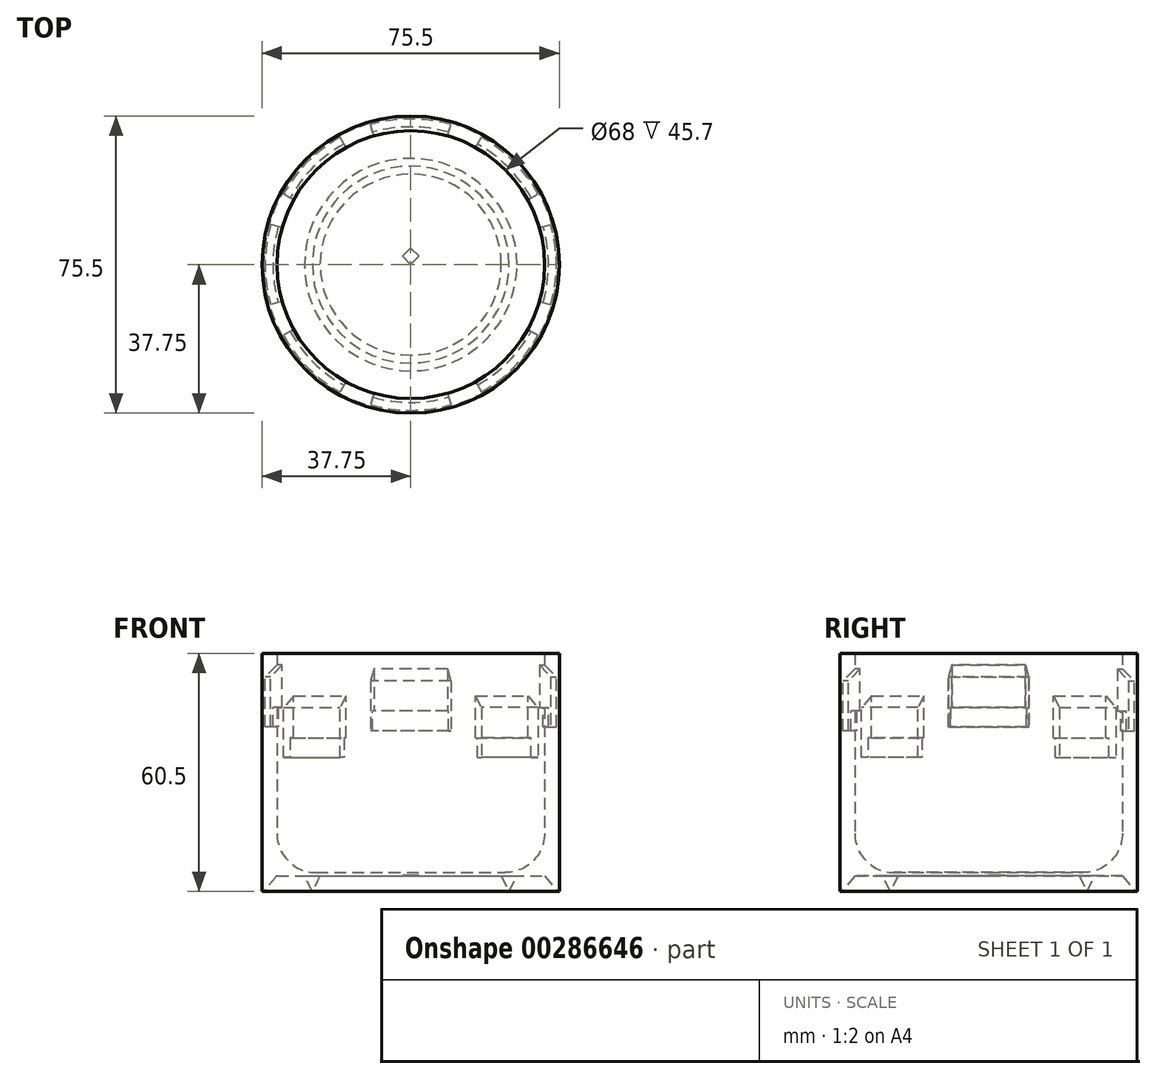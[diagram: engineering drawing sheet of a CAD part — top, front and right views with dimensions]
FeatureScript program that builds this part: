
annotation { "Feature Type Name" : "Feature", "Feature Type Description" : "" }
export const myFeature = defineFeature(function(context is Context, id is Id, definition is map)
    precondition{}
    {
        {
            var Q0;
            Q0=qCreatedBy(makeId("Front.planeOp"),FACE);
            var sketch = newSketch(context, id + "F0", { "sketchPlane" : qUnion([Q0])});
            skLineSegment(sketch, "E0", {"start": v(-34, 0) * mm, "end": v(-34, -4) * mm});
            skLineSegment(sketch, "E1", {"start": v(-34, -4) * mm, "end": v(-40, -4) * mm});
            skLineSegment(sketch, "E2", {"start": v(-40, -4) * mm, "end": v(-40, 21) * mm});
            skLineSegment(sketch, "E3", {"start": v(-34, 21) * mm, "end": v(-34, 0) * mm});
            skLineSegment(sketch, "E4", {"start": v(-34, 53) * mm, "end": v(0, 53) * mm, "construction": true});
            skArc(sketch, "E5", {"start": v(-34, 53) * mm, "mid": v(-24.04, 28.96) * mm, "end": v(0, 19) * mm, "construction": true});
            skLineSegment(sketch, "E6", {"start": v(-34, 19) * mm, "end": v(0, 19) * mm, "construction": true});
            skLineSegment(sketch, "E7", {"start": v(-34, 53) * mm, "end": v(-34, 48.5) * mm});
            skLineSegment(sketch, "E8", {"start": v(-34, 48.5) * mm, "end": v(0, 48.5) * mm, "construction": true});
            skArc(sketch, "E9", {"start": v(-34, 48.5) * mm, "mid": v(-22.6, 27.2) * mm, "end": v(0, 18.7) * mm});
            skArc(sketch, "E10", {"start": v(-34, 43.52) * mm, "mid": v(-21.35, 24.89) * mm, "end": v(0, 17.7) * mm, "construction": true});
            skPoint(sketch, "E11", {"position": v(-34, 43.52) * mm});
            skLineSegment(sketch, "E12", {"start": v(0, 18.7) * mm, "end": v(0, 17.7) * mm, "construction": true});
            skLineSegment(sketch, "E13", {"start": v(-34, 48.5) * mm, "end": v(-37, 48.5) * mm, "construction": true});
            skLineSegment(sketch, "E14", {"start": v(-37, 48.5) * mm, "end": v(-37, 37.8) * mm});
            skPoint(sketch, "E15", {"position": v(-37, 43.15) * mm});
            skLineSegment(sketch, "E16", {"start": v(-37, 54.5) * mm, "end": v(-34, 54.5) * mm, "construction": true});
            skLineSegment(sketch, "E17", {"start": v(-34, 54.5) * mm, "end": v(-34, 53) * mm});
            skLineSegment(sketch, "E18", {"start": v(-34, 43.52) * mm, "end": v(-35, 43.52) * mm, "construction": true});
            skLineSegment(sketch, "E19", {"start": v(-35, 41.8) * mm, "end": v(-35, 43.52) * mm, "construction": true});
            skPoint(sketch, "E20", {"position": v(-5, 19.07) * mm});
            skPoint(sketch, "E21", {"position": v(-5, 17.55) * mm});
            skLineSegment(sketch, "E22", {"start": v(-5, 19.07) * mm, "end": v(-5, 17.55) * mm});
            skLineSegment(sketch, "E23", {"start": v(0, 18.7) * mm, "end": v(0, 17.5) * mm});
            skArc(sketch, "E24", {"start": v(-34, 42.8) * mm, "mid": v(-21.19, 24.52) * mm, "end": v(0, 17.5) * mm, "construction": true});
            skLineSegment(sketch, "E25", {"start": v(-34, 42.8) * mm, "end": v(-35, 42.8) * mm});
            skLineSegment(sketch, "E26", {"start": v(-35, 41.8) * mm, "end": v(-35, 42.8) * mm});
            skLineSegment(sketch, "E27", {"start": v(-35, 41.8) * mm, "end": v(-35, 37.8) * mm});
            skLineSegment(sketch, "E28", {"start": v(-35, 37.8) * mm, "end": v(-37, 37.8) * mm});
            skLineSegment(sketch, "E29", {"start": v(-37, 54.5) * mm, "end": v(-37, 51.5) * mm, "construction": true});
            skLineSegment(sketch, "E30", {"start": v(-34, 42.8) * mm, "end": v(-34, 43.52) * mm, "construction": true});
            skLineSegment(sketch, "E31", {"start": v(-34, 21) * mm, "end": v(-34, 44.8) * mm});
            skLineSegment(sketch, "E32", {"start": v(-37, 51.5) * mm, "end": v(-34, 54.5) * mm, "construction": true});
            skLineSegment(sketch, "E33", {"start": v(-37, 48.5) * mm, "end": v(-37, 51.5) * mm});
            skLineSegment(sketch, "E34", {"start": v(60.14, 148.59) * mm, "end": v(60.14, 144.09) * mm});
            skArc(sketch, "E35", {"start": v(60.14, 144.09) * mm, "mid": v(71.54, 122.8) * mm, "end": v(94.14, 114.3) * mm});
            skArc(sketch, "E36", {"start": v(60.14, 139.11) * mm, "mid": v(72.8, 120.48) * mm, "end": v(94.14, 113.3) * mm, "construction": true});
            skPoint(sketch, "E37", {"position": v(60.14, 139.11) * mm});
            skLineSegment(sketch, "E38", {"start": v(94.14, 114.3) * mm, "end": v(94.14, 113.3) * mm, "construction": true});
            skLineSegment(sketch, "E39", {"start": v(60.14, 144.09) * mm, "end": v(57.14, 144.09) * mm});
            skLineSegment(sketch, "E40", {"start": v(57.14, 144.09) * mm, "end": v(57.14, 133.4) * mm});
            skPoint(sketch, "E41", {"position": v(57.14, 138.74) * mm});
            skLineSegment(sketch, "E42", {"start": v(57.14, 150.09) * mm, "end": v(60.14, 150.09) * mm, "construction": true});
            skLineSegment(sketch, "E43", {"start": v(60.14, 150.09) * mm, "end": v(60.14, 148.59) * mm});
            skLineSegment(sketch, "E44", {"start": v(60.14, 139.11) * mm, "end": v(59.14, 139.11) * mm, "construction": true});
            skLineSegment(sketch, "E45", {"start": v(59.14, 137.4) * mm, "end": v(59.14, 139.11) * mm, "construction": true});
            skPoint(sketch, "E46", {"position": v(89.14, 114.66) * mm});
            skPoint(sketch, "E47", {"position": v(89.14, 113.14) * mm});
            skLineSegment(sketch, "E48", {"start": v(89.14, 114.66) * mm, "end": v(89.14, 113.14) * mm});
            skLineSegment(sketch, "E49", {"start": v(94.14, 114.3) * mm, "end": v(94.14, 113.1) * mm});
            skArc(sketch, "E50", {"start": v(60.14, 138.4) * mm, "mid": v(72.96, 120.11) * mm, "end": v(94.14, 113.1) * mm});
            skLineSegment(sketch, "E51", {"start": v(60.14, 138.4) * mm, "end": v(59.14, 138.4) * mm});
            skLineSegment(sketch, "E52", {"start": v(59.14, 137.4) * mm, "end": v(59.14, 138.4) * mm});
            skLineSegment(sketch, "E53", {"start": v(59.14, 137.4) * mm, "end": v(59.14, 133.4) * mm});
            skLineSegment(sketch, "E54", {"start": v(59.14, 133.4) * mm, "end": v(57.14, 133.4) * mm});
            skLineSegment(sketch, "E55", {"start": v(59.14, 138.4) * mm, "end": v(57.14, 138.4) * mm});
            skLineSegment(sketch, "E56", {"start": v(57.14, 150.09) * mm, "end": v(57.14, 147.09) * mm, "construction": true});
            skLineSegment(sketch, "E57", {"start": v(60.14, 138.4) * mm, "end": v(60.14, 139.11) * mm, "construction": true});
            skLineSegment(sketch, "E58", {"start": v(57.14, 147.09) * mm, "end": v(60.14, 150.09) * mm});
            skLineSegment(sketch, "E59", {"start": v(57.14, 144.09) * mm, "end": v(57.14, 147.09) * mm});
            skLineSegment(sketch, "E60", {"start": v(-40, 21) * mm, "end": v(-40, 56.5) * mm});
            skLineSegment(sketch, "E61", {"start": v(-34, 37.8) * mm, "end": v(-34, 36.8) * mm});
            skLineSegment(sketch, "E62", {"start": v(-34, 42.8) * mm, "end": v(-34, 48.5) * mm});
            skLineSegment(sketch, "E63", {"start": v(0, 0) * mm, "end": v(0, 55) * mm, "construction": true});
            skLineSegment(sketch, "E64", {"start": v(-34, 54.5) * mm, "end": v(-34, 53.5) * mm});
            skLineSegment(sketch, "E65", {"start": v(-34, 53.5) * mm, "end": v(-37, 50.5) * mm});
            skLineSegment(sketch, "E66", {"start": v(-34, 53.5) * mm, "end": v(-37, 53.5) * mm});
            skLineSegment(sketch, "E67", {"start": v(-40, 56.5) * mm, "end": v(-34, 56.5) * mm});
            skLineSegment(sketch, "E68.MirrorCS", {"start": v(34, 53.5) * mm, "end": v(37, 50.5) * mm});
            skLineSegment(sketch, "E69.MirrorCS", {"start": v(37, 48.5) * mm, "end": v(37, 50.5) * mm});
            skLineSegment(sketch, "E70.MirrorCS", {"start": v(37, 48.5) * mm, "end": v(37, 37.8) * mm});
            skLineSegment(sketch, "E71.MirrorCS", {"start": v(35, 37.8) * mm, "end": v(37, 37.8) * mm});
            skLineSegment(sketch, "E72.MirrorCS", {"start": v(35, 41.8) * mm, "end": v(35, 37.8) * mm});
            skLineSegment(sketch, "E73.MirrorCS", {"start": v(34, 42.8) * mm, "end": v(35, 42.8) * mm});
            skLineSegment(sketch, "E74.MirrorCS", {"start": v(34, 42.8) * mm, "end": v(34, 48.5) * mm});
            skLineSegment(sketch, "E75.MirrorCS", {"start": v(34, 53) * mm, "end": v(34, 48.5) * mm});
            skLineSegment(sketch, "E76.MirrorCS", {"start": v(34, 53.5) * mm, "end": v(34, 53) * mm});
            skLineSegment(sketch, "E77", {"start": v(35, 41.8) * mm, "end": v(35, 42.8) * mm});
            skPoint(sketch, "E78.orphan", {"position": v(34, 54.5) * mm});
            skPoint(sketch, "E79.orphan", {"position": v(37, 51.5) * mm});
            skLineSegment(sketch, "E80", {"start": v(37, 39.8) * mm, "end": v(37, 0) * mm});
            skLineSegment(sketch, "E81", {"start": v(37, 0) * mm, "end": v(0, 0) * mm});
            skLineSegment(sketch, "E82", {"start": v(-5, 17.55) * mm, "end": v(-34, 17.55) * mm, "construction": true});
            skLineSegment(sketch, "E83", {"start": v(-40, 56.5) * mm, "end": v(-40, 96) * mm});
            skLineSegment(sketch, "E84", {"start": v(-40, 96) * mm, "end": v(-34, 96) * mm});
            skLineSegment(sketch, "E85", {"start": v(-34, 96) * mm, "end": v(-34, 56.5) * mm});
            skLineSegment(sketch, "E86", {"start": v(-34, 0) * mm, "end": v(0, 0) * mm});
            skLineSegment(sketch, "E87", {"start": v(0, 0) * mm, "end": v(0, 0.8) * mm});
            skLineSegment(sketch, "E88", {"start": v(0, 0.8) * mm, "end": v(-34, 0.8) * mm});
            skLineSegment(sketch, "E89", {"start": v(-34, 44.8) * mm, "end": v(-34, 42.8) * mm});
            skLineSegment(sketch, "E90", {"start": v(-34, 54.5) * mm, "end": v(-34, 56.5) * mm});
            skLineSegment(sketch, "E91", {"start": v(37, 39.8) * mm, "end": v(37, 31.97) * mm});
            skLineSegment(sketch, "E92", {"start": v(-40, -4) * mm, "end": v(-37.75, -4) * mm});
            skLineSegment(sketch, "E93", {"start": v(-37.75, -4) * mm, "end": v(-37.75, 96) * mm});
            skLineSegment(sketch, "E94", {"start": v(-37.75, -4) * mm, "end": v(-37.35, -4) * mm});
            skLineSegment(sketch, "E95", {"start": v(-37.35, -4) * mm, "end": v(-34, 0) * mm});
            skLineSegment(sketch, "E96", {"start": v(-34, 0) * mm, "end": v(-27, 0) * mm});
            skLineSegment(sketch, "E97", {"start": v(-25, -4) * mm, "end": v(-23, -4) * mm});
            skLineSegment(sketch, "E98", {"start": v(-27, 0) * mm, "end": v(-25, -4) * mm});
            skLineSegment(sketch, "E99", {"start": v(-25, -4) * mm, "end": v(-23, 0) * mm});
            skLineSegment(sketch, "E100", {"start": v(-34, 0) * mm, "end": v(-24, 0) * mm});
            skLineSegment(sketch, "E101", {"start": v(-24, 0) * mm, "end": v(-24, 10.8) * mm});
            skArc(sketch, "E102", {"start": v(-34, 10.8) * mm, "mid": v(-31.07, 3.73) * mm, "end": v(-24, 0.8) * mm});
            skSolve(sketch);
        }
        {
            var Q0;
            Q0=makeQuery(id+"F0.imprint","IMPRINT",FACE,{"disambiguationData":[TD([[makeQuery(id+"F0.imprint","IMPRINT",EDGE,{"derivedFrom":sQuery(id+"F0.wireOp",EDGE,"E7")}),-1.0]])]});
            var Q1;
            {var subQ7=sQuery(id+"F0.wireOp",EDGE,"E14");Q1=makeQuery(id+"F0.imprint","IMPRINT",FACE,{"disambiguationData":[TD([[makeQuery(id+"F0.imprint","IMPRINT",EDGE,{"derivedFrom":subQ7}),-1.0]])]});}
            var Q2;
            {var subQ0=sQuery(id+"F0.wireOp",EDGE,"E87");Q2=makeQuery(id+"F0.imprint","IMPRINT",FACE,{"disambiguationData":[TD([[makeQuery(id+"F0.imprint","IMPRINT",EDGE,{"derivedFrom":subQ0}),1.0]])]});}
            var Q3;
            {var subQ0=sQuery(id+"F0.wireOp",EDGE,"E98");Q3=makeQuery(id+"F0.imprint","IMPRINT",FACE,{"disambiguationData":[TD([[makeQuery(id+"F0.imprint","IMPRINT",EDGE,{"derivedFrom":subQ0}),1.0]])]});}
            var Q4;
            {var subQ3=sQuery(id+"F0.wireOp",EDGE,"E102");Q4=makeQuery(id+"F0.imprint","IMPRINT",FACE,{"disambiguationData":[TD([[makeQuery(id+"F0.imprint","IMPRINT",EDGE,{"derivedFrom":subQ3}),-1.0]])]});}
            var Q5;
            {var subQ4=sQuery(id+"F0.wireOp",EDGE,"E3");var subQ6=sQuery(id+"F0.wireOp",EDGE,"E88");var subQ7=makeQuery(id+"F0.imprint","INTERSECT",VERTEX,{"derivedFrom":[subQ4,subQ6]});Q5=makeQuery(id+"F0.imprint","IMPRINT",FACE,{"disambiguationData":[TD([[makeQuery(id+"F0.imprint","IMPRINT",EDGE,{"disambiguationData":[TD([[subQ7,1.0]])],"derivedFrom":subQ6}),1.0]])]});}
            var Q6;
            Q6=sQuery(id+"F0.wireOp",EDGE,"E63");
            revolve(context, id + "F1", {"entities" : qUnion([Q0, Q1, Q2, Q3, Q4, Q5]), "axis" : qUnion([Q6]), "revolveType" : RevolveType.FULL});
        }
        {
            var Q0;
            Q0=makeQuery(id+"F0.imprint","IMPRINT",FACE,{"disambiguationData":[TD([[makeQuery(id+"F0.imprint","IMPRINT",EDGE,{"derivedFrom":sQuery(id+"F0.wireOp",EDGE,"E7")}),-1.0]])]});
            var Q1;
            Q1=makeQuery(id+"F0.imprint","IMPRINT",FACE,{"disambiguationData":[TD([[makeQuery(id+"F0.imprint","IMPRINT",EDGE,{"derivedFrom":sQuery(id+"F0.wireOp",EDGE,"E68.MirrorCS")}),-1.0]])]});
            var Q2;
            Q2=sQuery(id+"F0.wireOp",EDGE,"E63");
            revolve(context, id + "F2", {"operationType" : NewBodyOperationType.REMOVE, "entities" : qUnion([Q0, Q1]), "axis" : qUnion([Q2]), "revolveType" : RevolveType.SYMMETRIC, "oppositeDirection" : true, "angle" : 32 * degree});
        }
        {
            var Q0;
            Q0=qCreatedBy(makeId("Right.planeOp"),FACE);
            var sketch = newSketch(context, id + "F3", { "sketchPlane" : qUnion([Q0])});
            skLineSegment(sketch, "E103", {"start": v(0, 20.7) * mm, "end": v(0, 19.7) * mm, "construction": true});
            skPoint(sketch, "E104", {"position": v(-5, 21.07) * mm});
            skPoint(sketch, "E105", {"position": v(-5, 19.55) * mm});
            skLineSegment(sketch, "E106", {"start": v(0, 20.7) * mm, "end": v(0, 19.5) * mm});
            skLineSegment(sketch, "E107", {"start": v(0, 0) * mm, "end": v(0, 55) * mm, "construction": true});
            skLineSegment(sketch, "E108.MirrorCS", {"start": v(34, 52.5) * mm, "end": v(37, 49.5) * mm});
            skLineSegment(sketch, "E109.MirrorCS", {"start": v(37, 47.5) * mm, "end": v(37, 49.5) * mm});
            skLineSegment(sketch, "E110.MirrorCS", {"start": v(37, 47.5) * mm, "end": v(37, 36.8) * mm});
            skLineSegment(sketch, "E111.MirrorCS", {"start": v(35, 36.8) * mm, "end": v(37, 36.8) * mm});
            skLineSegment(sketch, "E112.MirrorCS", {"start": v(35, 40.8) * mm, "end": v(35, 36.8) * mm});
            skLineSegment(sketch, "E113.MirrorCS", {"start": v(34, 41.8) * mm, "end": v(35, 41.8) * mm});
            skLineSegment(sketch, "E114.MirrorCS", {"start": v(34, 41.8) * mm, "end": v(34, 47.5) * mm});
            skLineSegment(sketch, "E115.MirrorCS", {"start": v(34, 52) * mm, "end": v(34, 47.5) * mm});
            skLineSegment(sketch, "E116.MirrorCS", {"start": v(34, 52.5) * mm, "end": v(34, 52) * mm});
            skLineSegment(sketch, "E117", {"start": v(35, 40.8) * mm, "end": v(35, 41.8) * mm});
            skPoint(sketch, "E118.orphan", {"position": v(34, 53.5) * mm});
            skPoint(sketch, "E119.orphan", {"position": v(37, 50.5) * mm});
            skLineSegment(sketch, "E120", {"start": v(37, 39.8) * mm, "end": v(37, 0) * mm});
            skLineSegment(sketch, "E121", {"start": v(37, 0) * mm, "end": v(0, 0) * mm});
            skLineSegment(sketch, "E122.MirrorCS", {"start": v(-34, 52.5) * mm, "end": v(-37, 49.5) * mm});
            skLineSegment(sketch, "E123.MirrorCS", {"start": v(-37, 47.5) * mm, "end": v(-37, 49.5) * mm});
            skLineSegment(sketch, "E124.MirrorCS", {"start": v(-35, 36.8) * mm, "end": v(-37, 36.8) * mm});
            skLineSegment(sketch, "E125.MirrorCS", {"start": v(-34, 52.5) * mm, "end": v(-34, 52) * mm});
            skLineSegment(sketch, "E126.MirrorCS", {"start": v(-35, 40.8) * mm, "end": v(-35, 36.8) * mm});
            skLineSegment(sketch, "E127.MirrorCS", {"start": v(-34, 41.8) * mm, "end": v(-35, 41.8) * mm});
            skLineSegment(sketch, "E128.MirrorCS", {"start": v(-35, 40.8) * mm, "end": v(-35, 41.8) * mm});
            skPoint(sketch, "E129.MirrorP", {"position": v(-37, 50.5) * mm});
            skPoint(sketch, "E130.MirrorP", {"position": v(-34, 53.5) * mm});
            skLineSegment(sketch, "E131.MirrorCS", {"start": v(-37, 47.5) * mm, "end": v(-37, 36.8) * mm});
            skLineSegment(sketch, "E132.MirrorCS", {"start": v(-34, 52) * mm, "end": v(-34, 47.5) * mm});
            skLineSegment(sketch, "E133.MirrorCS", {"start": v(-34, 41.8) * mm, "end": v(-34, 47.5) * mm});
            skLineSegment(sketch, "E134", {"start": v(37, 39.8) * mm, "end": v(37, 34.23) * mm});
            skLineSegment(sketch, "E135", {"start": v(37, 0) * mm, "end": v(37, 36.8) * mm});
            skLineSegment(sketch, "E136", {"start": v(35, 36.8) * mm, "end": v(-37, 36.8) * mm, "construction": true});
            skSolve(sketch);
        }
        {
            var Q0;
            Q0=makeQuery(id+"F3.imprint","IMPRINT",FACE,{"disambiguationData":[TD([[makeQuery(id+"F3.imprint","IMPRINT",EDGE,{"derivedFrom":sQuery(id+"F3.wireOp",EDGE,"E122.MirrorCS")}),1.0]])]});
            var Q1;
            Q1=makeQuery(id+"F3.imprint","IMPRINT",FACE,{"disambiguationData":[TD([[makeQuery(id+"F3.imprint","IMPRINT",EDGE,{"derivedFrom":sQuery(id+"F3.wireOp",EDGE,"E108.MirrorCS")}),-1.0]])]});
            var Q2;
            Q2=sQuery(id+"F3.wireOp",EDGE,"E107");
            revolve(context, id + "F4", {"operationType" : NewBodyOperationType.REMOVE, "entities" : qUnion([Q0, Q1]), "axis" : qUnion([Q2]), "revolveType" : RevolveType.SYMMETRIC, "oppositeDirection" : true, "angle" : 32 * degree});
        }
        {
            var Q0;
            Q0=qCreatedBy(makeId("Top.planeOp"),FACE);
            var sketch = newSketch(context, id + "F5", { "sketchPlane" : qUnion([Q0])});
            skLineSegment(sketch, "E137", {"start": v(20, 20) * mm, "end": v(0, 0) * mm});
            skLineSegment(sketch, "E138", {"start": v(0, 0) * mm, "end": v(-15.77, -15.77) * mm});
            skLineSegment(sketch, "E139", {"start": v(20, 20) * mm, "end": v(17.87, 22.13) * mm});
            skLineSegment(sketch, "E140", {"start": v(17.87, 22.13) * mm, "end": v(-17.64, -13.38) * mm});
            skLineSegment(sketch, "E141", {"start": v(-17.64, -13.38) * mm, "end": v(-15.77, -15.77) * mm});
            skLineSegment(sketch, "E142", {"start": v(0, 0) * mm, "end": v(0, 16.65) * mm});
            skLineSegment(sketch, "E143.MirrorCS", {"start": v(-20, 20) * mm, "end": v(0, 0) * mm});
            skLineSegment(sketch, "E144.MirrorCS", {"start": v(0, 0) * mm, "end": v(15.77, -15.77) * mm});
            skLineSegment(sketch, "E145.MirrorCS", {"start": v(-17.87, 22.13) * mm, "end": v(17.64, -13.38) * mm});
            skLineSegment(sketch, "E146.MirrorCS", {"start": v(17.64, -13.38) * mm, "end": v(15.77, -15.77) * mm});
            skLineSegment(sketch, "E147.MirrorCS", {"start": v(-20, 20) * mm, "end": v(-17.87, 22.13) * mm});
            skSolve(sketch);
        }
        {
            var Q0;
            Q0=makeQuery(id+"F5.imprint","IMPRINT",FACE,{"disambiguationData":[TD([[makeQuery(id+"F5.imprint","IMPRINT",EDGE,{"derivedFrom":sQuery(id+"F5.wireOp",EDGE,"E137")}),-1.0]])]});
            var Q1;
            {var subQ0=sQuery(id+"F5.wireOp",EDGE,"E143.MirrorCS");var subQ1=sQuery(id+"F5.wireOp",EDGE,"E140");var subQ2=makeQuery(id+"F5.imprint","INTERSECT",VERTEX,{"derivedFrom":[subQ1,subQ0]});Q1=makeQuery(id+"F5.imprint","IMPRINT",FACE,{"disambiguationData":[TD([[makeQuery(id+"F5.imprint","IMPRINT",EDGE,{"disambiguationData":[TD([[subQ2,1.0]])],"derivedFrom":subQ1}),1.0]])]});}
            extrude(context, id + "F6", {"entities" : qUnion([Q0, Q1]), "depth" : 0.1 * mm});
        }
        {
            var Q0;
            Q0=makeQuery(id+"F6.opExtrude","SWEPT_FACE",FACE,{"disambiguationData":[OSD([sQuery(id+"F5.wireOp",EDGE,"E137"),sQuery(id+"F5.wireOp",EDGE,"E138")])]});
            var sketch = newSketch(context, id + "F7", { "sketchPlane" : qUnion([Q0])});
            skLineSegment(sketch, "E148", {"start": v(0, 20.7) * mm, "end": v(0, 19.7) * mm, "construction": true});
            skPoint(sketch, "E149", {"position": v(-5, 21.07) * mm});
            skPoint(sketch, "E150", {"position": v(-5, 19.55) * mm});
            skLineSegment(sketch, "E151", {"start": v(0, 20.7) * mm, "end": v(0, 19.5) * mm});
            skLineSegment(sketch, "E152", {"start": v(0, 0) * mm, "end": v(0, 55) * mm, "construction": true});
            skLineSegment(sketch, "E153", {"start": v(37, 30) * mm, "end": v(37, -9.8) * mm});
            skLineSegment(sketch, "E154", {"start": v(37, 0) * mm, "end": v(0, 0) * mm});
            skLineSegment(sketch, "E155.MirrorCS", {"start": v(34, 45.7) * mm, "end": v(37, 42.7) * mm});
            skLineSegment(sketch, "E156.MirrorCS", {"start": v(37, 40.7) * mm, "end": v(37, 42.7) * mm});
            skLineSegment(sketch, "E157.MirrorCS", {"start": v(37, 40.7) * mm, "end": v(37, 30) * mm});
            skLineSegment(sketch, "E158.MirrorCS", {"start": v(35, 30) * mm, "end": v(37, 30) * mm});
            skLineSegment(sketch, "E159.MirrorCS", {"start": v(35, 34) * mm, "end": v(35, 30) * mm});
            skLineSegment(sketch, "E160.MirrorCS", {"start": v(34, 35) * mm, "end": v(35, 35) * mm});
            skLineSegment(sketch, "E161.MirrorCS", {"start": v(34, 35) * mm, "end": v(34, 40.7) * mm});
            skLineSegment(sketch, "E162.MirrorCS", {"start": v(34, 45.2) * mm, "end": v(34, 40.7) * mm});
            skLineSegment(sketch, "E163.MirrorCS", {"start": v(34, 45.7) * mm, "end": v(34, 45.2) * mm});
            skLineSegment(sketch, "E164", {"start": v(35, 34) * mm, "end": v(35, 35) * mm});
            skPoint(sketch, "E165.orphan", {"position": v(34, 46.7) * mm});
            skPoint(sketch, "E166.orphan", {"position": v(37, 43.7) * mm});
            skPoint(sketch, "E167.endSnap0", {"position": v(36, 30) * mm});
            skLineSegment(sketch, "E168.MirrorCS", {"start": v(-34, 45.7) * mm, "end": v(-34, 45.2) * mm});
            skLineSegment(sketch, "E169.MirrorCS", {"start": v(-35, 30) * mm, "end": v(-37, 30) * mm});
            skLineSegment(sketch, "E170.MirrorCS", {"start": v(-37, 40.7) * mm, "end": v(-37, 42.7) * mm});
            skLineSegment(sketch, "E171.MirrorCS", {"start": v(-35, 34) * mm, "end": v(-35, 35) * mm});
            skLineSegment(sketch, "E172.MirrorCS", {"start": v(-34, 35) * mm, "end": v(-35, 35) * mm});
            skLineSegment(sketch, "E173.MirrorCS", {"start": v(-34, 45.7) * mm, "end": v(-37, 42.7) * mm});
            skPoint(sketch, "E174.MirrorP", {"position": v(-37, 43.7) * mm});
            skLineSegment(sketch, "E175.MirrorCS", {"start": v(-34, 45.2) * mm, "end": v(-34, 40.7) * mm});
            skLineSegment(sketch, "E176.MirrorCS", {"start": v(-35, 34) * mm, "end": v(-35, 30) * mm});
            skPoint(sketch, "E177.MirrorP", {"position": v(-34, 46.7) * mm});
            skLineSegment(sketch, "E178.MirrorCS", {"start": v(-34, 35) * mm, "end": v(-34, 40.7) * mm});
            skLineSegment(sketch, "E179.MirrorCS", {"start": v(-37, 40.7) * mm, "end": v(-37, 30) * mm});
            skPoint(sketch, "E180.MirrorP", {"position": v(-36, 30) * mm});
            skLineSegment(sketch, "E181", {"start": v(35, 30) * mm, "end": v(-37, 30) * mm, "construction": true});
            skSolve(sketch);
        }
        {
            var Q0;
            Q0=makeQuery(id+"F7.imprint","IMPRINT",FACE,{"disambiguationData":[TD([[makeQuery(id+"F7.imprint","IMPRINT",EDGE,{"derivedFrom":sQuery(id+"F7.wireOp",EDGE,"E168.MirrorCS")}),-1.0]])]});
            var Q1;
            Q1=makeQuery(id+"F7.imprint","IMPRINT",FACE,{"disambiguationData":[TD([[makeQuery(id+"F7.imprint","IMPRINT",EDGE,{"derivedFrom":sQuery(id+"F7.wireOp",EDGE,"E158.MirrorCS")}),1.0]])]});
            var Q2;
            Q2=sQuery(id+"F7.wireOp",EDGE,"E152");
            revolve(context, id + "F8", {"operationType" : NewBodyOperationType.REMOVE, "entities" : qUnion([Q0, Q1]), "axis" : qUnion([Q2]), "revolveType" : RevolveType.SYMMETRIC, "oppositeDirection" : true, "angle" : 32 * degree});
        }
        {
            var Q0;
            Q0=makeQuery(id+"F6.opExtrude","SWEPT_FACE",FACE,{"disambiguationData":[OSD([sQuery(id+"F5.wireOp",EDGE,"E143.MirrorCS")])]});
            var sketch = newSketch(context, id + "F9", { "sketchPlane" : qUnion([Q0])});
            skLineSegment(sketch, "E182", {"start": v(0, 20.7) * mm, "end": v(0, 19.7) * mm, "construction": true});
            skPoint(sketch, "E183", {"position": v(-5, 21.07) * mm});
            skPoint(sketch, "E184", {"position": v(-5, 19.55) * mm});
            skLineSegment(sketch, "E185", {"start": v(0, 20.7) * mm, "end": v(0, 19.5) * mm});
            skLineSegment(sketch, "E186", {"start": v(0, 0) * mm, "end": v(0, 55) * mm, "construction": true});
            skLineSegment(sketch, "E187", {"start": v(37, 30) * mm, "end": v(37, -9.8) * mm});
            skLineSegment(sketch, "E188", {"start": v(37, 0) * mm, "end": v(0, 0) * mm});
            skLineSegment(sketch, "E189.MirrorCS", {"start": v(34, 45.7) * mm, "end": v(37, 42.7) * mm});
            skLineSegment(sketch, "E190.MirrorCS", {"start": v(37, 40.7) * mm, "end": v(37, 42.7) * mm});
            skLineSegment(sketch, "E191.MirrorCS", {"start": v(37, 40.7) * mm, "end": v(37, 30) * mm});
            skLineSegment(sketch, "E192.MirrorCS", {"start": v(35, 30) * mm, "end": v(37, 30) * mm});
            skLineSegment(sketch, "E193.MirrorCS", {"start": v(35, 34) * mm, "end": v(35, 30) * mm});
            skLineSegment(sketch, "E194.MirrorCS", {"start": v(34, 35) * mm, "end": v(35, 35) * mm});
            skLineSegment(sketch, "E195.MirrorCS", {"start": v(34, 35) * mm, "end": v(34, 40.7) * mm});
            skLineSegment(sketch, "E196.MirrorCS", {"start": v(34, 45.2) * mm, "end": v(34, 40.7) * mm});
            skLineSegment(sketch, "E197.MirrorCS", {"start": v(34, 45.7) * mm, "end": v(34, 45.2) * mm});
            skLineSegment(sketch, "E198", {"start": v(35, 34) * mm, "end": v(35, 35) * mm});
            skPoint(sketch, "E199.orphan", {"position": v(34, 46.7) * mm});
            skPoint(sketch, "E200.orphan", {"position": v(37, 43.7) * mm});
            skPoint(sketch, "E201.endSnap0", {"position": v(36, 30) * mm});
            skLineSegment(sketch, "E202.MirrorCS", {"start": v(-34, 45.7) * mm, "end": v(-34, 45.2) * mm});
            skLineSegment(sketch, "E203.MirrorCS", {"start": v(-35, 30) * mm, "end": v(-37, 30) * mm});
            skLineSegment(sketch, "E204.MirrorCS", {"start": v(-37, 40.7) * mm, "end": v(-37, 42.7) * mm});
            skLineSegment(sketch, "E205.MirrorCS", {"start": v(-35, 34) * mm, "end": v(-35, 35) * mm});
            skLineSegment(sketch, "E206.MirrorCS", {"start": v(-34, 35) * mm, "end": v(-35, 35) * mm});
            skLineSegment(sketch, "E207.MirrorCS", {"start": v(-34, 45.7) * mm, "end": v(-37, 42.7) * mm});
            skPoint(sketch, "E208.MirrorP", {"position": v(-37, 43.7) * mm});
            skLineSegment(sketch, "E209.MirrorCS", {"start": v(-34, 45.2) * mm, "end": v(-34, 40.7) * mm});
            skLineSegment(sketch, "E210.MirrorCS", {"start": v(-35, 34) * mm, "end": v(-35, 30) * mm});
            skPoint(sketch, "E211.MirrorP", {"position": v(-34, 46.7) * mm});
            skLineSegment(sketch, "E212.MirrorCS", {"start": v(-34, 35) * mm, "end": v(-34, 40.7) * mm});
            skLineSegment(sketch, "E213.MirrorCS", {"start": v(-37, 40.7) * mm, "end": v(-37, 30) * mm});
            skPoint(sketch, "E214.MirrorP", {"position": v(-36, 30) * mm});
            skLineSegment(sketch, "E215", {"start": v(35, 30) * mm, "end": v(-37, 30) * mm, "construction": true});
            skSolve(sketch);
        }
        {
            var Q0;
            Q0=makeQuery(id+"F9.imprint","IMPRINT",FACE,{"disambiguationData":[TD([[makeQuery(id+"F9.imprint","IMPRINT",EDGE,{"derivedFrom":sQuery(id+"F9.wireOp",EDGE,"E202.MirrorCS")}),-1.0]])]});
            var Q1;
            Q1=makeQuery(id+"F9.imprint","IMPRINT",FACE,{"disambiguationData":[TD([[makeQuery(id+"F9.imprint","IMPRINT",EDGE,{"derivedFrom":sQuery(id+"F9.wireOp",EDGE,"E192.MirrorCS")}),1.0]])]});
            var Q2;
            Q2=sQuery(id+"F9.wireOp",EDGE,"E186");
            revolve(context, id + "F10", {"operationType" : NewBodyOperationType.REMOVE, "entities" : qUnion([Q0, Q1]), "axis" : qUnion([Q2]), "revolveType" : RevolveType.SYMMETRIC, "oppositeDirection" : true, "angle" : 32 * degree});
        }
    });
